# Revit family: LINEAL 36W_LKB0956WW_CW
name_source: partatom
category: Luminarias
units: mm (PartAtom-declared; Revit-internal decimal feet)

## family parameters
Compartido = No
Corte con vacíos al cargar = No
Cota de conector redondo = Diámetro de uso
Origen de luz = Sí
Punto de cálculo de habitación = No
Se basa en plano de trabajo = Sí
Siempre vertical = No
Tipo de pieza = Normal

## types (2) — shared parameters
Archivo de red fotométrica = LKB0956 WW.IES
Cambio de temperatura de color de luz atenuada = <Ninguno>
Comentarios de vataje = 100-277V
Fabricante = BRILLANT
Filtro de color = 16777215
Longitud de línea de emisión = 200 mm
Lámpara = OSRAM
Watt per fixture = 36
Ángulo de inclinación = 25.00°
zero-valued in all types: Elevación por defecto

## per-type parameters (varying)
| type | Descripción | Modelo |
| EMP_LKB0956WW.30 | LUMINARIA PARA EMPOTRAR TIPO LINEAL CON 24 LED TIPO OSRAM CON UNA POTENCIA DE 36W, CUERPO DE ALUMINIO EXTRUIDO CUBIERTO CON POLVO GRIS OSCURO CON CUBIERTA DE ACERO INOXIDABLE Y VIDRIO TEMPLADO DE 6MM, HOUSING DE ALUMINIO, CON UNA DIMENSION DE 80MM DE PROFUNDO POR 1007 DE LARGO EN LA LUMINARIA, CUENTA CON 2055 LUMENES A UNA TEMPERATURA EN BLANCO CALIDO DE 3000K, CORRIENTE DE OPERACIÓN A 312mA, ON/OFF, DIMEABLE EN TRIAC, CABLE H05RN L0.5M, IRC 80, IK07, IP67, ANGULO DE APERTURA A 30 GRADOS EN STOCK, ALIMENTADA A 100-277V. | LKB0956WW.30 |
| EMP_LKB0956CW | LUMINARIA PARA EMPOTRAR TIPO LINEAL CON 24 LED TIPO OSRAM CON UNA POTENCIA DE 36W, CUERPO DE ALUMINIO EXTRUIDO CUBIERTO CON POLVO GRIS OSCURO CON CUBIERTA DE ACERO INOXIDABLE Y VIDRIO TEMPLADO DE 6MM, HOUSING DE ALUMINIO, CON UNA DIMENSION DE 80MM DE PROFUNDO POR 1007 DE LARGO EN LA LUMINARIA, CUENTA CON 2198 LUMENES A UNA TEMPERATURA EN BLANCO FRIO DE 6000K, CORRIENTE DE OPERACIÓN A 312mA, ON/OFF, DIMEABLE EN TRIAC, CABLE H05RN L0.5M, IRC 80, IK07, IP67, ANGULO DE APERTURA A 30 GRADOS EN STOCK, ALIMENTADA A 100-277V. | LKB0956CW |

## geometry (parser evidence)
native form markers: Blend x2
no freeform markers — native parametric forms only
